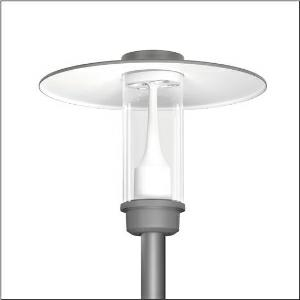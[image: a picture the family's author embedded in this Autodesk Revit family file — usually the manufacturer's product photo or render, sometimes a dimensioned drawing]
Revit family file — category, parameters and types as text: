
# Revit family: litepole_2_iq___st1_2a_5xa5425ef14hp_0eb2
name_source: partatom
category: Lighting Fixtures
units: mm (PartAtom-declared; Revit-internal decimal feet)

## family parameters
Cut with Voids When Loaded = No
Host = Face
Light Source = No
Part Type = Normal
Room Calculation Point = No
Round Connector Dimension = Use Diameter
Shared = No

## types (1)
- --- (1 x LED, 4760 lm, 33.6 W, 3000K)
    Apparent Load = 34 VA
    CIE Flux Codes = 22 59 92 98 100
    Color Rendering = 70
    Color Temperature = 3000K
    Default Elevation = 1800 mm
    Description = Litepole 2 iQ, mast luminaire, Module 540 iQ-SR, primary light control with 3 zone facetted reflector, of plastic, silver coated, highly specular, structured, primary optical cover: cover, of PMMA, transparent, light distribution: ST1.2a, light emission: direct distribution, primary light characteristic: asymmetric, installation type: post-top, LED, High Power LED, rated luminous flux: 4.760lm, luminous efficacy: 142lm/W, light colour: 730, colour temperature: 3000K, control gear: iQ Street-Remote, control: pre-setting: logarithmic dimming characteristic, Street-Remote, Auto-Match, Temp-Guard, Lumen-Switch, Night-Set, Smart-Wire, Light-Fading, Desk-Remote (wireless, voltage-free reading and setting of iQ features in the workshop via application-optimized NFC function/RFID function), optimised constant luminous flux control (CLO 2.0), with terminal, 6-pole, max. 2.5mm², mains connection: 230..240V, AC, 50/60Hz, start of lifetime: 34W, end of service life: 36W, reduction: 15W, luminaire housing, upper part, of aluminium, coated, Siteco® metallic grey (DB 702S), diameter: 750mm, height: 590mm, spigot size: d x l = 76 x 70mm (post-top) | with reducer (optional accessory) 60 x 70mm, mounting height: 3..5m, post-top mast mounting element, of diecast aluminium, coated, Siteco® metallic grey (DB 702S), Module 540 iQ-SR, traffic white (RAL 9016), equipment: Power, protection rating (complete): IP65, insulation class (complete): insulation class II (safety insulation), certification: CE, ENEC, VDE, packaging unit: 1 piece

Light Distribution: ST1.2a
    Height = 590 mm
    Lamp = 1 x LED
    Lamp Light Flux = 4760 lm
    Lamp Power = 33.6 W
    Lamp count = 1
    Length = 750 mm
    Luminous efficacy = 142 lm/W
    Manufacturer = Siteco
    ModVariant = No
    Model = 5XA5425EF14HP
    Number of Poles = 1
    OnlyDefault = Yes
    Power Factor = 1
    Product Name = Litepole 2 iQ | ST1.2a
    Product group = mast luminaire | pylon top
    ProductGroupID = 6100
    Protection Class = Protection class II
    Protection Degree = IP 65
    RLX_Detail_Level = 1
    RLX_Emergency_Light_Flux = 0 lm
    RLX_Emergency_Type = 0
    RLX_Emergency_Type_DB = No
    RlxData = <blob elided: 31913 chars, md5=0e6f3a25>
    Socket = socket
    Standby Power = 0 W
    System Light Flux = 4760 lm
    System Power = 34 W
    Type Comments = factory setting: luminous flux: 100 % | dim-lin: 254 | 695 mA
    Type Image = l_1006518.jpg
    URL = http://relux.com
    VarID = @adj_213559
    Voltage = 0 V
    Weight = 0.00 kg
    Width = 0 mm  [stored 0 ft]

note: [stored X ft] marks values corroborated as IEEE doubles in the binary element streams (Revit-internal decimal feet)

## geometry (parser evidence)
native form markers: Blend x4, Sweep x11
no freeform markers — native parametric forms only
